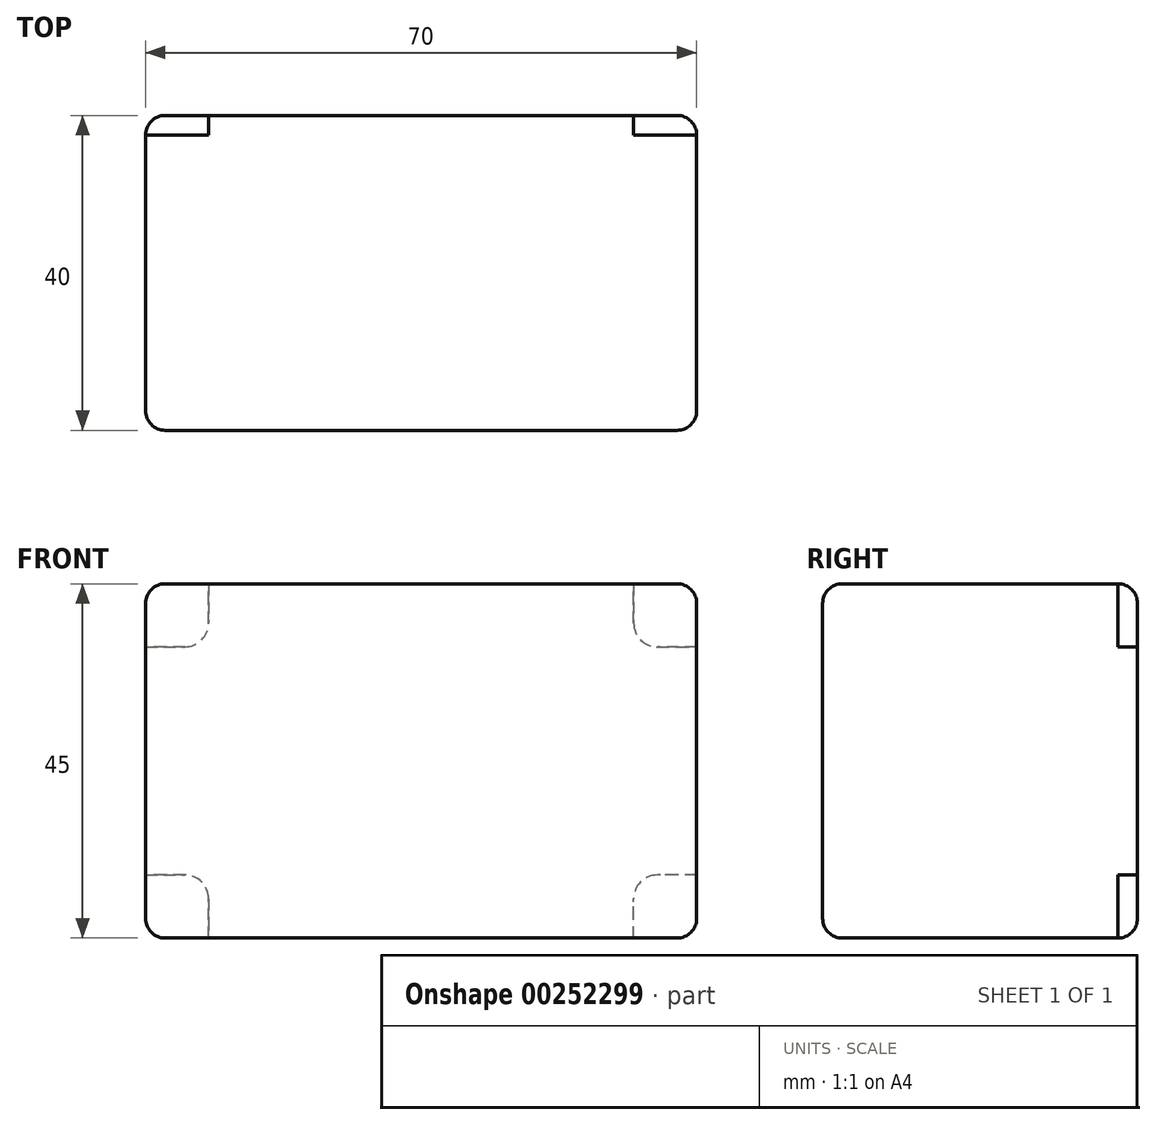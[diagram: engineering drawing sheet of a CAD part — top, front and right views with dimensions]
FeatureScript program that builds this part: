
annotation { "Feature Type Name" : "Feature", "Feature Type Description" : "" }
export const myFeature = defineFeature(function(context is Context, id is Id, definition is map)
    precondition{}
    {
        {
            var Q0;
            Q0=qCreatedBy(makeId("Front.planeOp"),FACE);
            var sketch = newSketch(context, id + "F0", { "sketchPlane" : qUnion([Q0])});
            skLineSegment(sketch, "E0.bottom", {"start": v(35, 22.5) * mm, "end": v(-35, 22.5) * mm});
            skLineSegment(sketch, "E0.top", {"start": v(35, -22.5) * mm, "end": v(-35, -22.5) * mm});
            skLineSegment(sketch, "E0.left", {"start": v(35, 22.5) * mm, "end": v(35, -22.5) * mm});
            skLineSegment(sketch, "E0.right", {"start": v(-35, 22.5) * mm, "end": v(-35, -22.5) * mm});
            skPoint(sketch, "E0.middle", {"position": v(0, 0) * mm});
            skSolve(sketch);
        }
        {
            var Q0;
            Q0=makeQuery(id+"F0.imprint","IMPRINT",FACE,{"disambiguationData":[TD([[makeQuery(id+"F0.imprint","IMPRINT",EDGE,{"derivedFrom":sQuery(id+"F0.wireOp",EDGE,"E0.bottom")}),1.0]])]});
            extrude(context, id + "F1", {"entities" : qUnion([Q0]), "endBound" : BoundingType.SYMMETRIC, "depth" : 40 * mm});
        }
        {
            var Q0;
            Q0=makeQuery(id+"F1.opExtrude","CAP_FACE",FACE,{"disambiguationData":[OSD([sQuery(id+"F0.wireOp",EDGE,"E0.bottom"),sQuery(id+"F0.wireOp",EDGE,"E0.top"),sQuery(id+"F0.wireOp",EDGE,"E0.left"),sQuery(id+"F0.wireOp",EDGE,"E0.right")])],"isStart":true});
            var sketch = newSketch(context, id + "F2", { "sketchPlane" : qUnion([Q0])});
            skLineSegment(sketch, "E1.bottom", {"start": v(-35, -22.5) * mm, "end": v(-27, -22.5) * mm});
            skLineSegment(sketch, "E1.top", {"start": v(-35, -14.5) * mm, "end": v(-27, -14.5) * mm});
            skLineSegment(sketch, "E1.left", {"start": v(-35, -22.5) * mm, "end": v(-35, -14.5) * mm});
            skLineSegment(sketch, "E1.right", {"start": v(-27, -22.5) * mm, "end": v(-27, -14.5) * mm});
            skSolve(sketch);
        }
        {
            var Q0;
            Q0=makeQuery(id+"F2.imprint","IMPRINT",FACE,{"disambiguationData":[TD([[makeQuery(id+"F2.imprint","IMPRINT",EDGE,{"derivedFrom":sQuery(id+"F2.wireOp",EDGE,"E1.bottom")}),1.0]])]});
            extrude(context, id + "F3", {"entities" : qUnion([Q0]), "operationType" : NewBodyOperationType.REMOVE, "endBound" : BoundingType.SYMMETRIC, "depth" : 5 * mm});
        }
        {
            var Q0;
            Q0=makeQuery(id+"F1.opExtrude","CAP_FACE",FACE,{"disambiguationData":[OSD([sQuery(id+"F0.wireOp",EDGE,"E0.bottom"),sQuery(id+"F0.wireOp",EDGE,"E0.top"),sQuery(id+"F0.wireOp",EDGE,"E0.left"),sQuery(id+"F0.wireOp",EDGE,"E0.right")])],"isStart":true});
            var sketch = newSketch(context, id + "F4", { "sketchPlane" : qUnion([Q0])});
            skLineSegment(sketch, "E2.bottom", {"start": v(35, -22.5) * mm, "end": v(27, -22.5) * mm});
            skLineSegment(sketch, "E2.top", {"start": v(35, -14.5) * mm, "end": v(27, -14.5) * mm});
            skLineSegment(sketch, "E2.left", {"start": v(35, -22.5) * mm, "end": v(35, -14.5) * mm});
            skLineSegment(sketch, "E2.right", {"start": v(27, -22.5) * mm, "end": v(27, -14.5) * mm});
            skSolve(sketch);
        }
        {
            var Q0;
            Q0=makeQuery(id+"F4.imprint","IMPRINT",FACE,{"disambiguationData":[TD([[makeQuery(id+"F4.imprint","IMPRINT",EDGE,{"derivedFrom":sQuery(id+"F4.wireOp",EDGE,"E2.bottom")}),1.0]])]});
            extrude(context, id + "F5", {"entities" : qUnion([Q0]), "operationType" : NewBodyOperationType.REMOVE, "endBound" : BoundingType.SYMMETRIC, "oppositeDirection" : true, "depth" : 5 * mm});
        }
        {
            var Q0;
            Q0=makeQuery(id+"F1.opExtrude","CAP_FACE",FACE,{"disambiguationData":[OSD([sQuery(id+"F0.wireOp",EDGE,"E0.bottom"),sQuery(id+"F0.wireOp",EDGE,"E0.top"),sQuery(id+"F0.wireOp",EDGE,"E0.left"),sQuery(id+"F0.wireOp",EDGE,"E0.right")])],"isStart":true});
            var sketch = newSketch(context, id + "F6", { "sketchPlane" : qUnion([Q0])});
            skLineSegment(sketch, "E3.bottom", {"start": v(-35, 22.5) * mm, "end": v(-27, 22.5) * mm});
            skLineSegment(sketch, "E3.top", {"start": v(-35, 14.5) * mm, "end": v(-27, 14.5) * mm});
            skLineSegment(sketch, "E3.left", {"start": v(-35, 22.5) * mm, "end": v(-35, 14.5) * mm});
            skLineSegment(sketch, "E3.right", {"start": v(-27, 22.5) * mm, "end": v(-27, 14.5) * mm});
            skSolve(sketch);
        }
        {
            var Q0;
            Q0=makeQuery(id+"F6.imprint","IMPRINT",FACE,{"disambiguationData":[TD([[makeQuery(id+"F6.imprint","IMPRINT",EDGE,{"derivedFrom":sQuery(id+"F6.wireOp",EDGE,"E3.bottom")}),-1.0]])]});
            extrude(context, id + "F7", {"entities" : qUnion([Q0]), "operationType" : NewBodyOperationType.REMOVE, "endBound" : BoundingType.SYMMETRIC, "oppositeDirection" : true, "depth" : 5 * mm});
        }
        {
            var Q0;
            Q0=makeQuery(id+"F1.opExtrude","CAP_FACE",FACE,{"disambiguationData":[OSD([sQuery(id+"F0.wireOp",EDGE,"E0.bottom"),sQuery(id+"F0.wireOp",EDGE,"E0.top"),sQuery(id+"F0.wireOp",EDGE,"E0.left"),sQuery(id+"F0.wireOp",EDGE,"E0.right")])],"isStart":true});
            var sketch = newSketch(context, id + "F8", { "sketchPlane" : qUnion([Q0])});
            skLineSegment(sketch, "E4.bottom", {"start": v(35, 22.5) * mm, "end": v(27, 22.5) * mm});
            skLineSegment(sketch, "E4.top", {"start": v(35, 14.5) * mm, "end": v(27, 14.5) * mm});
            skLineSegment(sketch, "E4.left", {"start": v(35, 22.5) * mm, "end": v(35, 14.5) * mm});
            skLineSegment(sketch, "E4.right", {"start": v(27, 22.5) * mm, "end": v(27, 14.5) * mm});
            skSolve(sketch);
        }
        {
            var Q0;
            Q0=makeQuery(id+"F8.imprint","IMPRINT",FACE,{"disambiguationData":[TD([[makeQuery(id+"F8.imprint","IMPRINT",EDGE,{"derivedFrom":sQuery(id+"F8.wireOp",EDGE,"E4.bottom")}),-1.0]])]});
            extrude(context, id + "F9", {"entities" : qUnion([Q0]), "operationType" : NewBodyOperationType.REMOVE, "endBound" : BoundingType.SYMMETRIC, "oppositeDirection" : true, "depth" : 5 * mm});
        }
        {
            var Q0;
            Q0=makeQuery(id+"F1.opExtrude","SWEPT_EDGE",EDGE,{"disambiguationData":[OSD([sQuery(id+"F0.wireOp",EDGE,"E0.top"),sQuery(id+"F0.wireOp",EDGE,"E0.left")])]});
            var Q1;
            Q1=makeQuery(id+"F1.opExtrude","SWEPT_EDGE",EDGE,{"disambiguationData":[OSD([sQuery(id+"F0.wireOp",EDGE,"E0.bottom"),sQuery(id+"F0.wireOp",EDGE,"E0.left")])]});
            var Q2;
            Q2=makeQuery(id+"F1.opExtrude","SWEPT_EDGE",EDGE,{"disambiguationData":[OSD([sQuery(id+"F0.wireOp",EDGE,"E0.bottom"),sQuery(id+"F0.wireOp",EDGE,"E0.right")])]});
            var Q3;
            Q3=makeQuery(id+"F1.opExtrude","SWEPT_EDGE",EDGE,{"disambiguationData":[OSD([sQuery(id+"F0.wireOp",EDGE,"E0.top"),sQuery(id+"F0.wireOp",EDGE,"E0.right")])]});
            var Q4;
            Q4=makeQuery(id+"F1.opExtrude","CAP_EDGE",EDGE,{"disambiguationData":[OSD([sQuery(id+"F0.wireOp",EDGE,"E0.right")])],"isStart":false});
            var Q5;
            Q5=makeQuery(id+"F1.opExtrude","CAP_EDGE",EDGE,{"disambiguationData":[OSD([sQuery(id+"F0.wireOp",EDGE,"E0.right")])],"isStart":true});
            var Q6;
            Q6=makeQuery(id+"F1.opExtrude","CAP_EDGE",EDGE,{"disambiguationData":[OSD([sQuery(id+"F0.wireOp",EDGE,"E0.bottom")])],"isStart":true});
            var Q7;
            Q7=makeQuery(id+"F1.opExtrude","CAP_EDGE",EDGE,{"disambiguationData":[OSD([sQuery(id+"F0.wireOp",EDGE,"E0.left")])],"isStart":true});
            var Q8;
            Q8=makeQuery(id+"F1.opExtrude","CAP_EDGE",EDGE,{"disambiguationData":[OSD([sQuery(id+"F0.wireOp",EDGE,"E0.top")])],"isStart":true});
            var Q9;
            Q9=makeQuery(id+"F1.opExtrude","CAP_EDGE",EDGE,{"disambiguationData":[OSD([sQuery(id+"F0.wireOp",EDGE,"E0.bottom")])],"isStart":false});
            var Q10;
            Q10=makeQuery(id+"F1.opExtrude","CAP_EDGE",EDGE,{"disambiguationData":[OSD([sQuery(id+"F0.wireOp",EDGE,"E0.top")])],"isStart":false});
            var Q11;
            Q11=makeQuery(id+"F1.opExtrude","CAP_EDGE",EDGE,{"disambiguationData":[OSD([sQuery(id+"F0.wireOp",EDGE,"E0.left")])],"isStart":false});
            fillet(context, id + "F10", {"entities" : qUnion([Q0, Q1, Q2, Q3, Q4, Q5, Q6, Q7, Q8, Q9, Q10, Q11]), "radius" : 2.5 * mm, "tangentPropagation" : true, "allowEdgeOverflow" : false});
        }
        {
            var Q0;
            Q0=makeQuery(id+"F7.boolean.opBoolean","COPY",EDGE,{"derivedFrom":makeQuery(id+"F7.opExtrude","SWEPT_EDGE",EDGE,{"disambiguationData":[OSD([sQuery(id+"F6.wireOp",EDGE,"E3.top"),sQuery(id+"F6.wireOp",EDGE,"E3.right")])]})});
            var Q1;
            Q1=makeQuery(id+"F3.boolean.opBoolean","COPY",EDGE,{"derivedFrom":makeQuery(id+"F3.opExtrude","SWEPT_EDGE",EDGE,{"disambiguationData":[OSD([sQuery(id+"F2.wireOp",EDGE,"E1.top"),sQuery(id+"F2.wireOp",EDGE,"E1.right")])]})});
            var Q2;
            Q2=makeQuery(id+"F5.boolean.opBoolean","COPY",EDGE,{"derivedFrom":makeQuery(id+"F5.opExtrude","SWEPT_EDGE",EDGE,{"disambiguationData":[OSD([sQuery(id+"F4.wireOp",EDGE,"E2.top"),sQuery(id+"F4.wireOp",EDGE,"E2.right")])]})});
            var Q3;
            Q3=makeQuery(id+"F9.boolean.opBoolean","COPY",EDGE,{"derivedFrom":makeQuery(id+"F9.opExtrude","SWEPT_EDGE",EDGE,{"disambiguationData":[OSD([sQuery(id+"F8.wireOp",EDGE,"E4.top"),sQuery(id+"F8.wireOp",EDGE,"E4.right")])]})});
            fillet(context, id + "F11", {"entities" : qUnion([Q0, Q1, Q2, Q3]), "radius" : 3 * mm, "tangentPropagation" : true, "allowEdgeOverflow" : false});
        }
    });
